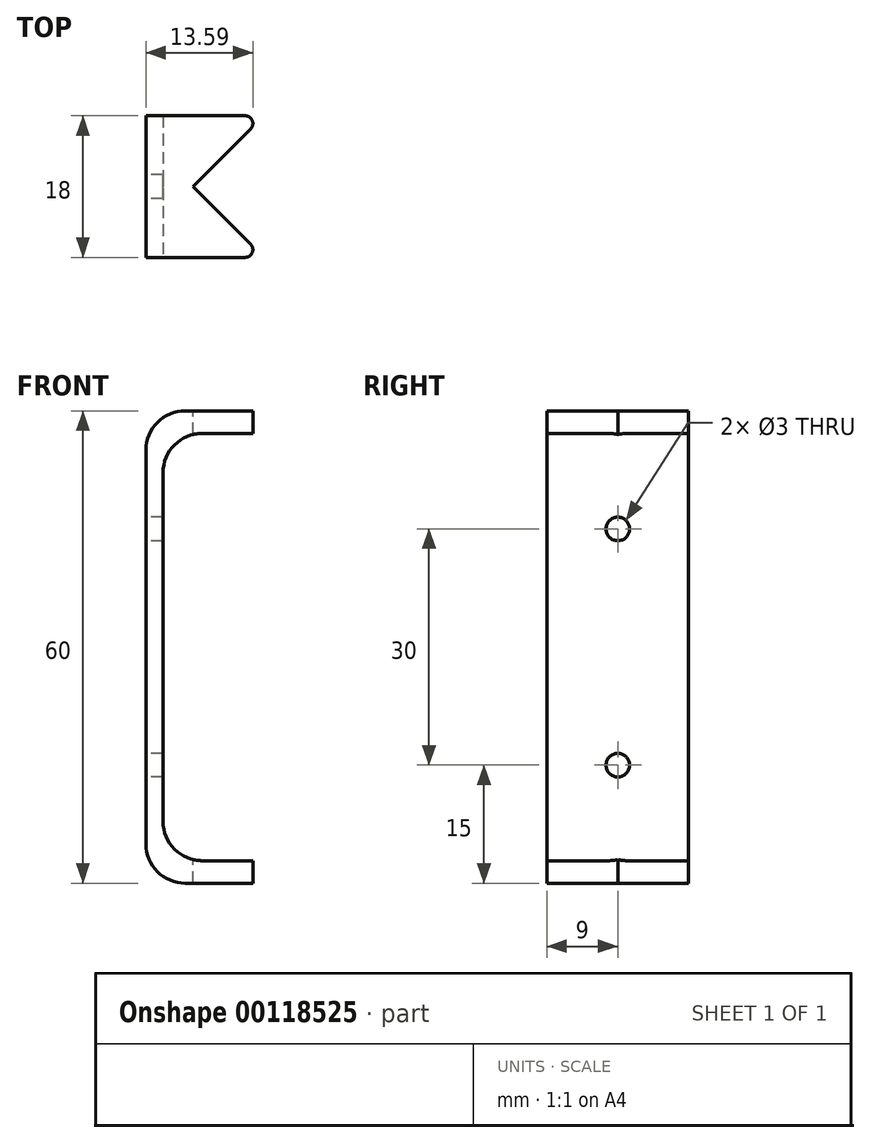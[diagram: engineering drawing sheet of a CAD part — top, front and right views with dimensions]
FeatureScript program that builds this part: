
annotation { "Feature Type Name" : "Feature", "Feature Type Description" : "" }
export const myFeature = defineFeature(function(context is Context, id is Id, definition is map)
    precondition{}
    {
        {
            var Q0;
            Q0=qCreatedBy(makeId("Right.planeOp"),FACE);
            var sketch = newSketch(context, id + "F0", { "sketchPlane" : qUnion([Q0])});
            skLineSegment(sketch, "E0.bottom", {"start": v(9, 30) * mm, "end": v(-9, 30) * mm});
            skLineSegment(sketch, "E0.top", {"start": v(9, -30) * mm, "end": v(-9, -30) * mm});
            skLineSegment(sketch, "E0.left", {"start": v(9, 30) * mm, "end": v(9, -30) * mm});
            skLineSegment(sketch, "E0.right", {"start": v(-9, 30) * mm, "end": v(-9, -30) * mm});
            skPoint(sketch, "E0.middle", {"position": v(0, 0) * mm});
            skCircle(sketch, "E1", {"center": v(0, 15) * mm, "radius": 1.5 * mm});
            skCircle(sketch, "E2", {"center": v(0, -15) * mm, "radius": 1.5 * mm});
            skSolve(sketch);
        }
        {
            var Q0;
            Q0=qSketchRegion(id+"F0",true);
            extrude(context, id + "F1", {"entities" : qUnion([Q0]), "depth" : 15 * mm});
        }
        {
            var Q0;
            Q0=makeQuery(id+"F1.opExtrude","SWEPT_FACE",FACE,{"disambiguationData":[OSD([sQuery(id+"F0.wireOp",EDGE,"E0.bottom")])]});
            var sketch = newSketch(context, id + "F2", { "sketchPlane" : qUnion([Q0])});
            skLineSegment(sketch, "E3", {"start": v(15, 9) * mm, "end": v(6, 0) * mm});
            skLineSegment(sketch, "E4", {"start": v(6, 0) * mm, "end": v(15, -9) * mm});
            skLineSegment(sketch, "E5", {"start": v(15, -9) * mm, "end": v(15, 9) * mm});
            skSolve(sketch);
        }
        {
            var Q0;
            Q0=qSketchRegion(id+"F2",true);
            extrude(context, id + "F3", {"entities" : qUnion([Q0]), "operationType" : NewBodyOperationType.REMOVE, "oppositeDirection" : true, "depth" : 80 * mm});
        }
        {
            var Q0;
            Q0=makeQuery(id+"F1.opExtrude","SWEPT_FACE",FACE,{"disambiguationData":[OSD([sQuery(id+"F0.wireOp",EDGE,"E0.right")])]});
            var sketch = newSketch(context, id + "F4", { "sketchPlane" : qUnion([Q0])});
            skLineSegment(sketch, "E6.bottom", {"start": v(15, -27.14) * mm, "end": v(2.18, -27.14) * mm});
            skLineSegment(sketch, "E6.top", {"start": v(15, 27.14) * mm, "end": v(2.18, 27.14) * mm});
            skLineSegment(sketch, "E6.left", {"start": v(15, -27.14) * mm, "end": v(15, 27.14) * mm});
            skLineSegment(sketch, "E6.right", {"start": v(2.18, -27.14) * mm, "end": v(2.18, 27.14) * mm});
            skPoint(sketch, "E6.middle", {"position": v(8.59, 0) * mm});
            skSolve(sketch);
        }
        {
            var Q0;
            Q0=qSketchRegion(id+"F4",true);
            extrude(context, id + "F5", {"entities" : qUnion([Q0]), "operationType" : NewBodyOperationType.REMOVE, "oppositeDirection" : true, "depth" : 25 * mm});
        }
        {
            var Q0;
            {var subQ0=sQuery(id+"F0.wireOp",EDGE,"E0.bottom");var subQ1=sQuery(id+"F0.wireOp",EDGE,"E0.right");var subQ2=sQuery(id+"F2.wireOp",EDGE,"E4");Q0=makeQuery(id+"F5.boolean.opBoolean","SPLIT",EDGE,{"disambiguationData":[TD([makeQuery(id+"F1.opExtrude","SWEPT_FACE",FACE,{"disambiguationData":[OSD([subQ0])]})])],"derivedFrom":makeQuery(id+"F3.boolean.opBoolean","MERGE",EDGE,{"derivedFrom":[makeQuery(id+"F1.opExtrude","CAP_EDGE",EDGE,{"disambiguationData":[OSD([subQ1])],"isStart":false}),makeQuery(id+"F3.opExtrude","SWEPT_EDGE",EDGE,{"disambiguationData":[OSD([subQ0,subQ1,subQ2,sQuery(id+"F2.wireOp",EDGE,"E5")])]})]})});}
            var Q1;
            {var subQ0=sQuery(id+"F0.wireOp",EDGE,"E0.bottom");var subQ1=sQuery(id+"F0.wireOp",EDGE,"E0.left");var subQ2=sQuery(id+"F2.wireOp",EDGE,"E3");Q1=makeQuery(id+"F5.boolean.opBoolean","SPLIT",EDGE,{"disambiguationData":[TD([makeQuery(id+"F1.opExtrude","SWEPT_FACE",FACE,{"disambiguationData":[OSD([subQ0])]})])],"derivedFrom":makeQuery(id+"F3.boolean.opBoolean","MERGE",EDGE,{"derivedFrom":[makeQuery(id+"F1.opExtrude","CAP_EDGE",EDGE,{"disambiguationData":[OSD([subQ1])],"isStart":false}),makeQuery(id+"F3.opExtrude","SWEPT_EDGE",EDGE,{"disambiguationData":[OSD([subQ0,subQ1,subQ2,sQuery(id+"F2.wireOp",EDGE,"E5")])]})]})});}
            var Q2;
            {var subQ0=sQuery(id+"F0.wireOp",EDGE,"E0.right");var subQ1=sQuery(id+"F2.wireOp",EDGE,"E4");Q2=makeQuery(id+"F5.boolean.opBoolean","SPLIT",EDGE,{"disambiguationData":[TD([makeQuery(id+"F1.opExtrude","SWEPT_FACE",FACE,{"disambiguationData":[OSD([sQuery(id+"F0.wireOp",EDGE,"E0.top")])]})])],"derivedFrom":makeQuery(id+"F3.boolean.opBoolean","MERGE",EDGE,{"derivedFrom":[makeQuery(id+"F1.opExtrude","CAP_EDGE",EDGE,{"disambiguationData":[OSD([subQ0])],"isStart":false}),makeQuery(id+"F3.opExtrude","SWEPT_EDGE",EDGE,{"disambiguationData":[OSD([sQuery(id+"F0.wireOp",EDGE,"E0.bottom"),subQ0,subQ1,sQuery(id+"F2.wireOp",EDGE,"E5")])]})]})});}
            var Q3;
            {var subQ0=sQuery(id+"F0.wireOp",EDGE,"E0.left");var subQ1=sQuery(id+"F2.wireOp",EDGE,"E3");Q3=makeQuery(id+"F5.boolean.opBoolean","SPLIT",EDGE,{"disambiguationData":[TD([makeQuery(id+"F1.opExtrude","SWEPT_FACE",FACE,{"disambiguationData":[OSD([sQuery(id+"F0.wireOp",EDGE,"E0.top")])]})])],"derivedFrom":makeQuery(id+"F3.boolean.opBoolean","MERGE",EDGE,{"derivedFrom":[makeQuery(id+"F1.opExtrude","CAP_EDGE",EDGE,{"disambiguationData":[OSD([subQ0])],"isStart":false}),makeQuery(id+"F3.opExtrude","SWEPT_EDGE",EDGE,{"disambiguationData":[OSD([sQuery(id+"F0.wireOp",EDGE,"E0.bottom"),subQ0,subQ1,sQuery(id+"F2.wireOp",EDGE,"E5")])]})]})});}
            fillet(context, id + "F6", {"entities" : qUnion([Q0, Q1, Q2, Q3]), "radius" : 1 * mm, "tangentPropagation" : true, "allowEdgeOverflow" : false});
        }
        {
            var Q0;
            Q0=makeQuery(id+"F1.opExtrude","CAP_EDGE",EDGE,{"disambiguationData":[OSD([sQuery(id+"F0.wireOp",EDGE,"E0.bottom")])],"isStart":true});
            var Q1;
            Q1=makeQuery(id+"F1.opExtrude","CAP_EDGE",EDGE,{"disambiguationData":[OSD([sQuery(id+"F0.wireOp",EDGE,"E0.top")])],"isStart":true});
            var Q2;
            Q2=makeQuery(id+"F5.boolean.opBoolean","COPY",EDGE,{"derivedFrom":makeQuery(id+"F5.opExtrude","SWEPT_EDGE",EDGE,{"disambiguationData":[OSD([sQuery(id+"F4.wireOp",EDGE,"E6.top"),sQuery(id+"F4.wireOp",EDGE,"E6.right")])]})});
            var Q3;
            Q3=makeQuery(id+"F5.boolean.opBoolean","COPY",EDGE,{"derivedFrom":makeQuery(id+"F5.opExtrude","SWEPT_EDGE",EDGE,{"disambiguationData":[OSD([sQuery(id+"F4.wireOp",EDGE,"E6.bottom"),sQuery(id+"F4.wireOp",EDGE,"E6.right")])]})});
            fillet(context, id + "F7", {"entities" : qUnion([Q0, Q1, Q2, Q3]), "radius" : 5 * mm, "tangentPropagation" : true, "allowEdgeOverflow" : false});
        }
    });
